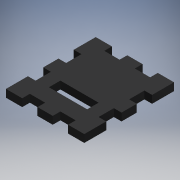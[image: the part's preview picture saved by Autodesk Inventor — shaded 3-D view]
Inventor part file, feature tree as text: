
AUTODESK INVENTOR PART (.ipt)
format: ipt  version: 2019 (Build 230136000, 136)  size: 166,912 bytes
history: native  units: mm
features: extrude x2, sketch x2
ambient origin geometry x8: Origin, YZ Plane, XZ Plane, XY Plane, X Axis, Y Axis, Z Axis, Center Point
bodies: Solid1 (feature_tree)
feature tree (4):
  extrude  "Extrusion1"  Depth=47.0mm
  extrude  "Extrusion2"  Depth=6.0mm
  sketch  "Sketch1"  dims[d0=41.0mm d1=47.0mm]
  sketch  "Sketch2"  dims[d2=20.0mm d3=6.0mm d4=10.5mm d5=12.0mm d6=4.0mm d7=0.0mm d8=4.0mm d9=8.0mm d10=4.0mm d11=8.0mm d12=4.0mm d13=4.0mm d14=0.0mm]
